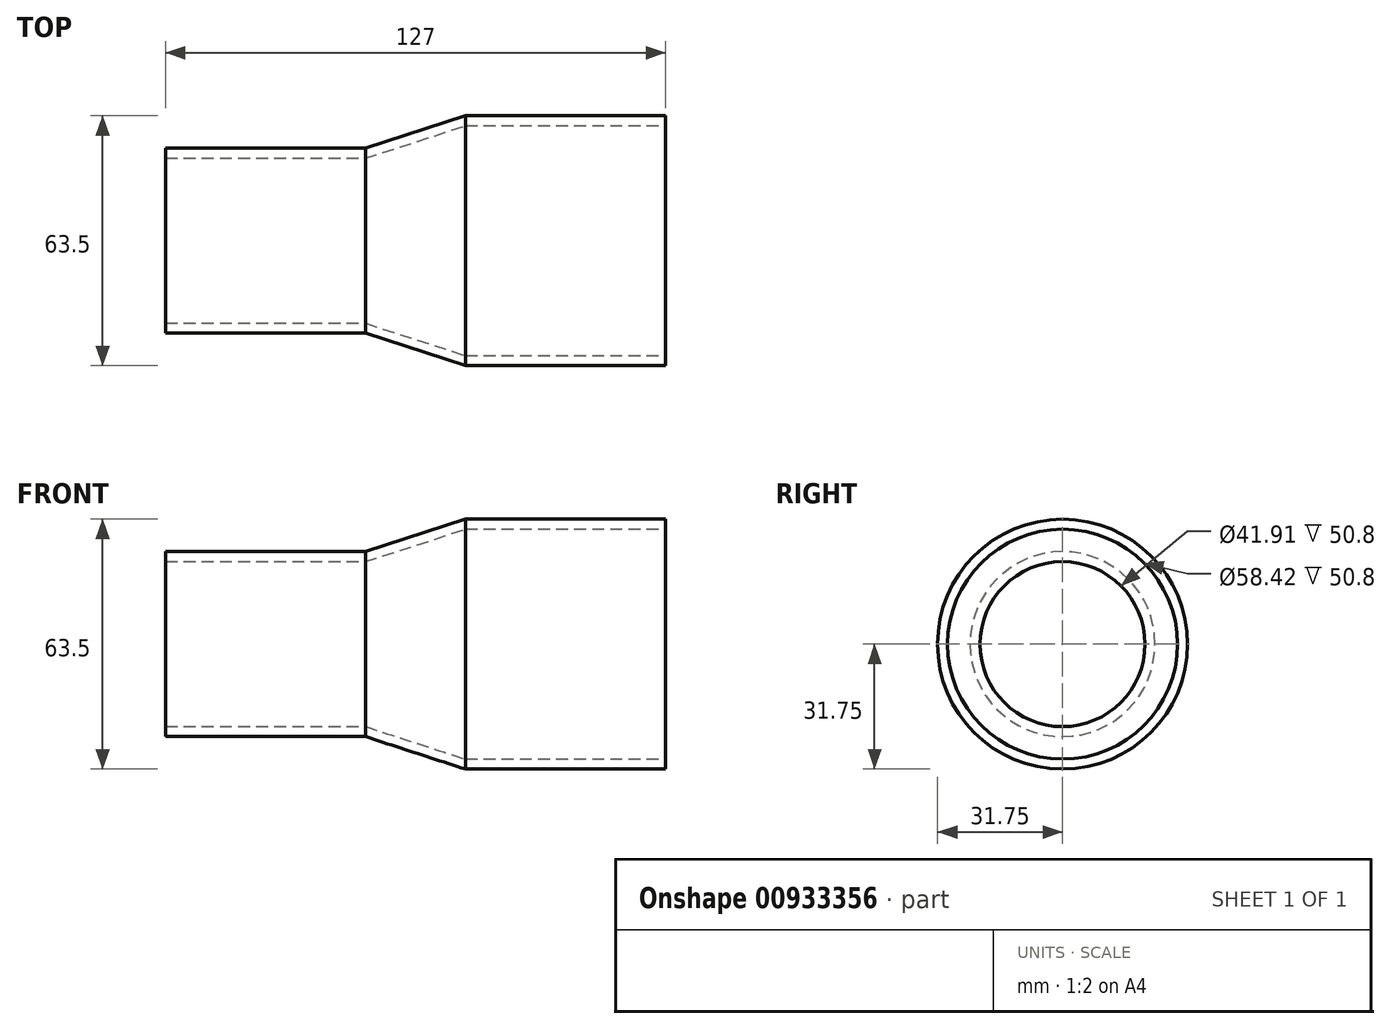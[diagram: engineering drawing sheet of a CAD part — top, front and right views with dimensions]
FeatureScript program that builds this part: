
annotation { "Feature Type Name" : "Feature", "Feature Type Description" : "" }
export const myFeature = defineFeature(function(context is Context, id is Id, definition is map)
    precondition{}
    {
        {
            var Q0;
            Q0=qCreatedBy(makeId("Front.planeOp"),FACE);
            var sketch = newSketch(context, id + "F0", { "sketchPlane" : qUnion([Q0])});
            skLineSegment(sketch, "E0", {"start": v(0, 0) * mm, "end": v(-90.9, 0) * mm, "construction": true});
            skLineSegment(sketch, "E1", {"start": v(0, 31.75) * mm, "end": v(50.8, 31.75) * mm});
            skLineSegment(sketch, "E2", {"start": v(50.8, 31.75) * mm, "end": v(50.8, 29.21) * mm});
            skLineSegment(sketch, "E3", {"start": v(50.8, 29.21) * mm, "end": v(0, 29.21) * mm});
            skLineSegment(sketch, "E4", {"start": v(0, 29.21) * mm, "end": v(-25.4, 20.96) * mm});
            skLineSegment(sketch, "E5", {"start": v(-25.4, 20.96) * mm, "end": v(-76.2, 20.95) * mm});
            skLineSegment(sketch, "E6", {"start": v(-76.2, 20.95) * mm, "end": v(-76.2, 23.5) * mm});
            skLineSegment(sketch, "E7", {"start": v(-76.2, 23.5) * mm, "end": v(-25.4, 23.5) * mm});
            skLineSegment(sketch, "E8", {"start": v(-25.4, 23.5) * mm, "end": v(0, 31.75) * mm});
            skPoint(sketch, "E9", {"position": v(25.4, 29.21) * mm});
            skPoint(sketch, "E10", {"position": v(-50.8, 20.96) * mm});
            skLineSegment(sketch, "E11", {"start": v(-25.4, 20.96) * mm, "end": v(-25.4, 23.5) * mm, "construction": true});
            skSolve(sketch);
        }
        {
            var Q0;
            Q0=qSketchRegion(id+"F0",true);
            var Q1;
            Q1=sQuery(id+"F0.wireOp",EDGE,"E0");
            revolve(context, id + "F1", {"surfaceOperationType" : NewSurfaceOperationType.NEW, "entities" : qUnion([Q0]), "axis" : qUnion([Q1]), "revolveType" : RevolveType.FULL});
        }
    });
